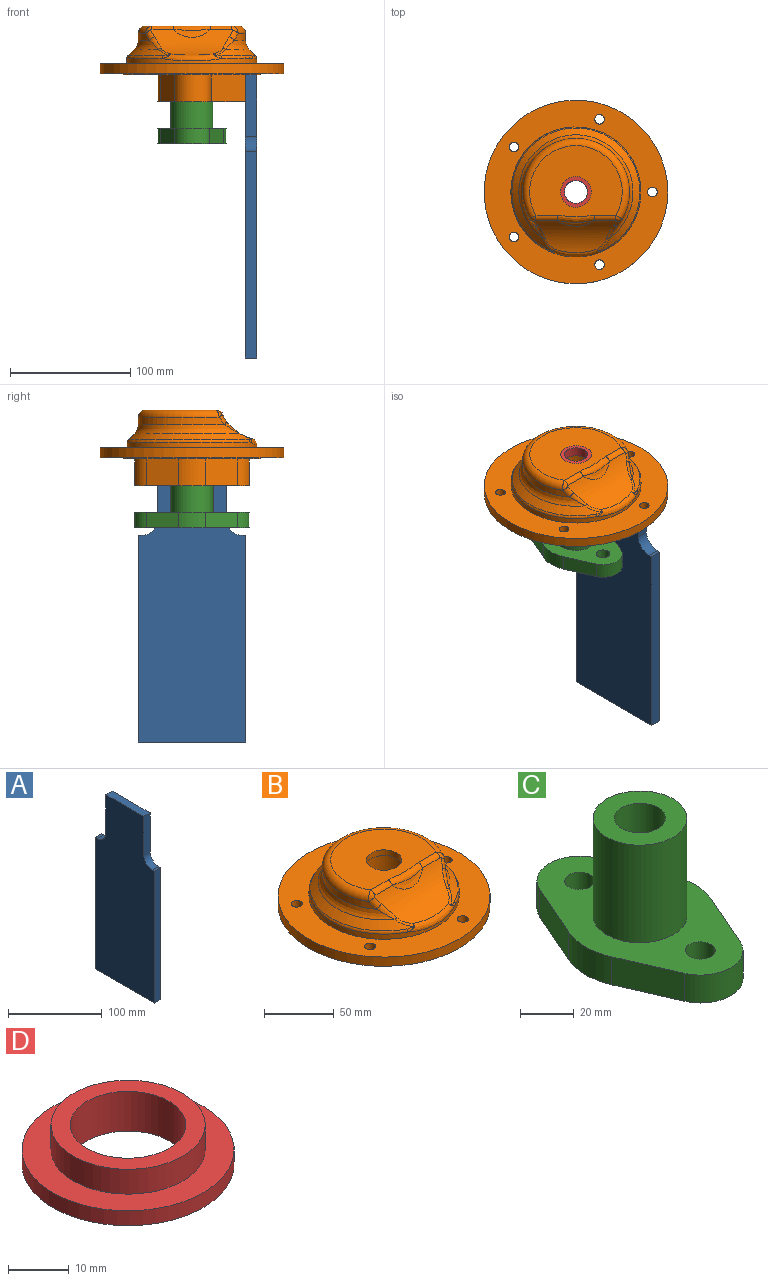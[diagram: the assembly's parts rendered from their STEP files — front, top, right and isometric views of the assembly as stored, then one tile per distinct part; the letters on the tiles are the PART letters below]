
ASSEMBLY  parts=4 mates=3
PART A: 12 faces, bbox 9.5x88.9x235 mm
  f0: plane 57.15x9.53mm, normal (0,0,1), area 544.4mm2, adj f1,f9,f10,f11
  f1: plane 50.8x9.53mm, normal (0,-1,0), area 483.9mm2, adj f0,f2,f10,f11
  f2: cylinder r=12.7mm len=12.7mm, axis (-1,0,0), area 190mm2, adj f1,f3,f10,f11
  f3: plane 9.53x3.18mm, normal (0,0,1), area 30.2mm2, adj f2,f4,f10,f11
  f4: plane 171.45x9.53mm, normal (0,-1,0), area 1633.1mm2, adj f3,f5,f10,f11
  f5: plane 88.9x9.53mm, normal (0,0,-1), area 846.8mm2, adj f4,f6,f10,f11
  f6: plane 171.45x9.53mm, normal (0,1,0), area 1633.1mm2, adj f5,f7,f10,f11
  f7: plane 9.53x3.18mm, normal (0,0,1), area 30.2mm2, adj f6,f8,f10,f11
  f8: cylinder r=12.7mm len=12.7mm, axis (-1,0,0), area 190mm2, adj f7,f9,f10,f11
  f9: plane 50.8x9.53mm, normal (0,1,0), area 483.9mm2, adj f0,f8,f10,f11
  f10: plane 234.95x88.9mm, normal (1,0,0), area 18940.2mm2, adj f0,f1,f2,f3,f4,f5,f6,f7
  f11: plane 234.95x88.9mm, normal (-1,0,0), area 18940.2mm2, adj f0,f1,f2,f3,f4,f5,f6,f7
PART B: 60 faces, bbox 152.4x152.4x68.5 mm
  f0: plane 114.3x113.9mm, normal (0,0,-1), area 5156.4mm2, adj f1,f2,f3,f4,f5,f19,f20,f21
  f1: cylinder r=57.15mm len=53.11mm, axis (0,0,1), area 58.3mm2, adj f0,f16,f38,f41
  f2: cylinder r=57.15mm len=45.17mm, axis (0,0,1), area 58.3mm2, adj f0,f16,f37,f40
  f3: cylinder r=57.15mm len=53.11mm, axis (0,0,1), area 58.3mm2, adj f0,f16,f39,f40
  f4: cylinder r=57.15mm len=55.84mm, axis (0,0,1), area 58.3mm2, adj f0,f16,f38,f39
  f5: cylinder r=57.15mm len=45.17mm, axis (0,0,1), area 58.3mm2, adj f0,f16,f37,f41
  f6: cylinder r=12.7mm len=25.4mm, axis (0,0,1), area 399mm2, adj f7,f18
  f7: plane 76.9x59.2mm, normal (0,0,1), area 3267.5mm2, adj f6,f8,f52,f54,f56
  f8: torus R=38.45mm, axis (0,0,1), area 1672.5mm2, adj f7,f9,f49,f58
  f9: cylinder r=44.45mm len=88.9mm, axis (0,0,1), area 1173.6mm2, adj f8,f10,f46,f59
  f10: torus R=54.45mm, axis (0,0,1), area 1698.1mm2, adj f9,f11,f44,f57
  f11: cone r=53.1mm half-angle=45deg, axis (0,0,-1), area 2160.2mm2, adj f10,f12,f45,f47,f50,f55
  f12: torus R=50.98mm, axis (0,0,1), area 675.7mm2, adj f11,f13,f47,f50
  f13: cylinder r=53.98mm len=107.95mm, axis (0,0,1), area 1526.1mm2, adj f12,f14,f51
  f14: plane 152.4x152.4mm, normal (0,0,1), area 8837.7mm2, adj f13,f15,f32,f33,f34,f35,f36
  f15: cylinder r=76.2mm len=152.4mm, axis (0,0,1), area 3878.1mm2, adj f14,f16
  f16: plane 152.4x152.4mm, normal (0,0,-1), area 7875.8mm2, adj f1,f2,f3,f4,f5,f15,f32,f33
  f17: cylinder r=17.46mm len=57.83mm, axis (0,0,1), area 6344.6mm2, adj f18,f29
  f18: plane 34.93x34.93mm, normal (0,0,-1), area 451.3mm2, adj f6,f17
  f19: plane 26.67x22.23mm, normal (-0.92,0.4,0), area 646.7mm2, adj f0,f20,f28,f29
  f20: cylinder r=15.88mm len=30.42mm, axis (0,0,1), area 1034.3mm2, adj f0,f19,f21,f29
  f21: plane 28.9x22.23mm, normal (0,1,0), area 642.2mm2, adj f0,f20,f22,f29
  f22: plane 57.15x22.23mm, normal (1,0,0), area 1270.2mm2, adj f0,f21,f23,f29
  f23: plane 28.9x22.23mm, normal (0,-1,0), area 642.2mm2, adj f0,f22,f24,f29
  f24: cylinder r=15.88mm len=30.42mm, axis (0,0,1), area 1034.3mm2, adj f0,f23,f25,f29
  f25: plane 26.67x22.23mm, normal (-0.92,-0.4,0), area 646.7mm2, adj f0,f24,f28,f29
  f26: cylinder r=5.56mm len=22.23mm, axis (0,0,1), area 775.9mm2, adj f29,f31
  f27: cylinder r=5.56mm len=22.23mm, axis (0,0,1), area 775.9mm2, adj f29,f30
  f28: cylinder r=28.57mm len=22.86mm, axis (0,0,1), area 522.7mm2, adj f0,f19,f25,f29
  f29: plane 95.25x73.03mm, normal (0,0,-1), area 3806mm2, adj f17,f19,f20,f21,f22,f23,f24,f25
  f30: plane 11.11x11.11mm, normal (0,0,-1), area 97mm2, adj f27
  f31: plane 11.11x11.11mm, normal (0,0,-1), area 97mm2, adj f26
  f32: cylinder r=4mm len=8.1mm, axis (0,0,-1), area 203.6mm2, adj f14,f16
  f33: cylinder r=4mm len=8.1mm, axis (0,0,-1), area 203.6mm2, adj f14,f16
  f34: cylinder r=4mm len=8.1mm, axis (0,0,-1), area 203.6mm2, adj f14,f16
  f35: cylinder r=4mm len=8.1mm, axis (0,0,-1), area 203.6mm2, adj f14,f16
  f36: cylinder r=4mm len=8.1mm, axis (0,0,-1), area 203.6mm2, adj f14,f16
  f37: cylinder r=9.53mm len=13.45mm, axis (0,0,1), area 14.9mm2, adj f0,f2,f5,f16
  f38: cylinder r=9.53mm len=10.88mm, axis (0,0,1), area 14.9mm2, adj f0,f1,f4,f16
  f39: cylinder r=9.53mm len=10.88mm, axis (0,0,1), area 14.9mm2, adj f0,f3,f4,f16
  f40: cylinder r=9.53mm len=12.79mm, axis (0,0,1), area 14.9mm2, adj f0,f2,f3,f16
  f41: cylinder r=9.53mm len=12.79mm, axis (0,0,1), area 14.9mm2, adj f0,f1,f5,f16
  f42: cylinder r=45.14mm len=67.94mm, axis (-1,0,0), area 1660mm2, adj f43,f44,f45,f46,f49,f51,f52,f55
  f43: bspline ~33.19x15.11mm, area 0mm2, adj f42,f54
  f44: bspline ~15.48x13.75mm, area 56.4mm2, adj f10,f42,f45,f46
  f45: bspline ~12.76x10.85mm, area 30.5mm2, adj f11,f42,f44,f48
  f46: bspline ~14.96x10.93mm, area 42.2mm2, adj f9,f42,f44,f49
  f47: bspline ~7.32x3.07mm, area 8.9mm2, adj f11,f12,f48,f51
  f48: bspline ~2.29x2.08mm, area 0.2mm2, adj f45,f47,f51
  f49: bspline ~6.41x5.95mm, area 26.4mm2, adj f8,f42,f46,f52
  f50: bspline ~8.66x3.62mm, area 8.9mm2, adj f11,f12,f51,f53
  f51: bspline ~55.8x10.82mm, area 262mm2, adj f13,f42,f47,f48,f50,f53
  f52: cylinder r=5mm len=17.8mm, axis (-1,0,0), area 95.3mm2, adj f7,f42,f49,f54
  f53: bspline ~2.29x2.07mm, area 0.2mm2, adj f50,f51,f55
  f54: bspline ~38.3x6.09mm, area 188.4mm2, adj f7,f43,f52,f56
  f55: bspline ~13.29x11.68mm, area 30.5mm2, adj f11,f42,f53,f57
  f56: cylinder r=5mm len=17.8mm, axis (-1,0,0), area 95.3mm2, adj f7,f42,f54,f58
  f57: bspline ~14.09x12.24mm, area 56.4mm2, adj f10,f42,f55,f59
  f58: bspline ~7.03x6.01mm, area 26.4mm2, adj f8,f42,f56,f59
  f59: bspline ~14.96x10.93mm, area 42.2mm2, adj f9,f42,f57,f58
PART C: 15 faces, bbox 57.2x95.3x57.2 mm
  f0: cylinder r=9.53mm len=57.15mm, axis (0,0,-1), area 3420.3mm2, adj f2,f13
  f1: cylinder r=17.46mm len=44.45mm, axis (0,0,-1), area 4877.1mm2, adj f2,f14
  f2: plane 34.93x34.93mm, normal (0,0,1), area 673mm2, adj f0,f1
  f3: cylinder r=28.57mm len=22.86mm, axis (0,0,1), area 298.7mm2, adj f4,f12,f13,f14
  f4: plane 26.67x12.7mm, normal (0.92,-0.4,0), area 369.6mm2, adj f3,f5,f13,f14
  f5: cylinder r=15.88mm len=29.1mm, axis (0,0,1), area 467.5mm2, adj f4,f6,f13,f14
  f6: plane 26.67x12.7mm, normal (-0.92,-0.4,0), area 369.6mm2, adj f5,f7,f13,f14
  f7: cylinder r=28.57mm len=22.86mm, axis (0,0,1), area 298.7mm2, adj f6,f8,f13,f14
  f8: plane 26.67x12.7mm, normal (-0.92,0.4,0), area 369.6mm2, adj f7,f9,f13,f14
  f9: cylinder r=15.88mm len=29.1mm, axis (0,0,1), area 467.5mm2, adj f8,f12,f13,f14
  f10: cylinder r=5.56mm len=12.7mm, axis (0,0,1), area 443.4mm2, adj f13,f14
  f11: cylinder r=5.56mm len=12.7mm, axis (0,0,1), area 443.4mm2, adj f13,f14
  f12: plane 26.67x12.7mm, normal (0.92,0.4,0), area 369.6mm2, adj f3,f9,f13,f14
  f13: plane 95.25x57.15mm, normal (0,0,-1), area 3364.3mm2, adj f0,f3,f4,f5,f6,f7,f8,f9
  f14: plane 95.25x57.15mm, normal (0,0,1), area 2691.3mm2, adj f1,f3,f4,f5,f6,f7,f8,f9
PART D: 6 faces, bbox 34.9x34.9x8 mm
  f0: cylinder r=17.46mm len=34.93mm, axis (0,0,1), area 329.2mm2, adj f1,f5
  f1: plane 34.93x34.93mm, normal (0,0,-1), area 673mm2, adj f0,f2
  f2: cylinder r=9.53mm len=19.05mm, axis (0,0,1), area 478.8mm2, adj f1,f3
  f3: plane 25.4x25.4mm, normal (0,0,1), area 221.7mm2, adj f2,f4
  f4: cylinder r=12.7mm len=25.4mm, axis (0,0,1), area 399mm2, adj f3,f5
  f5: plane 34.93x34.93mm, normal (0,0,1), area 451.3mm2, adj f0,f4
PLACE A t=(0,-152.4,0)mm
PLACE B at identity
PLACE C t=(0,-152.4,-3.17)mm
PLACE D at identity
MATE fastened D.f0 <-> B.f1  axis (0,0,1) through (0,-152.4,26.5)mm
MATE fastened C.f1 <-> B.f1  axis (0,0,-1) through (0,-152.4,-31.32)mm
MATE fastened A.f11 <-> B.f22  axis (-1,0,0) through (44.45,-152.4,-9.1)mm
